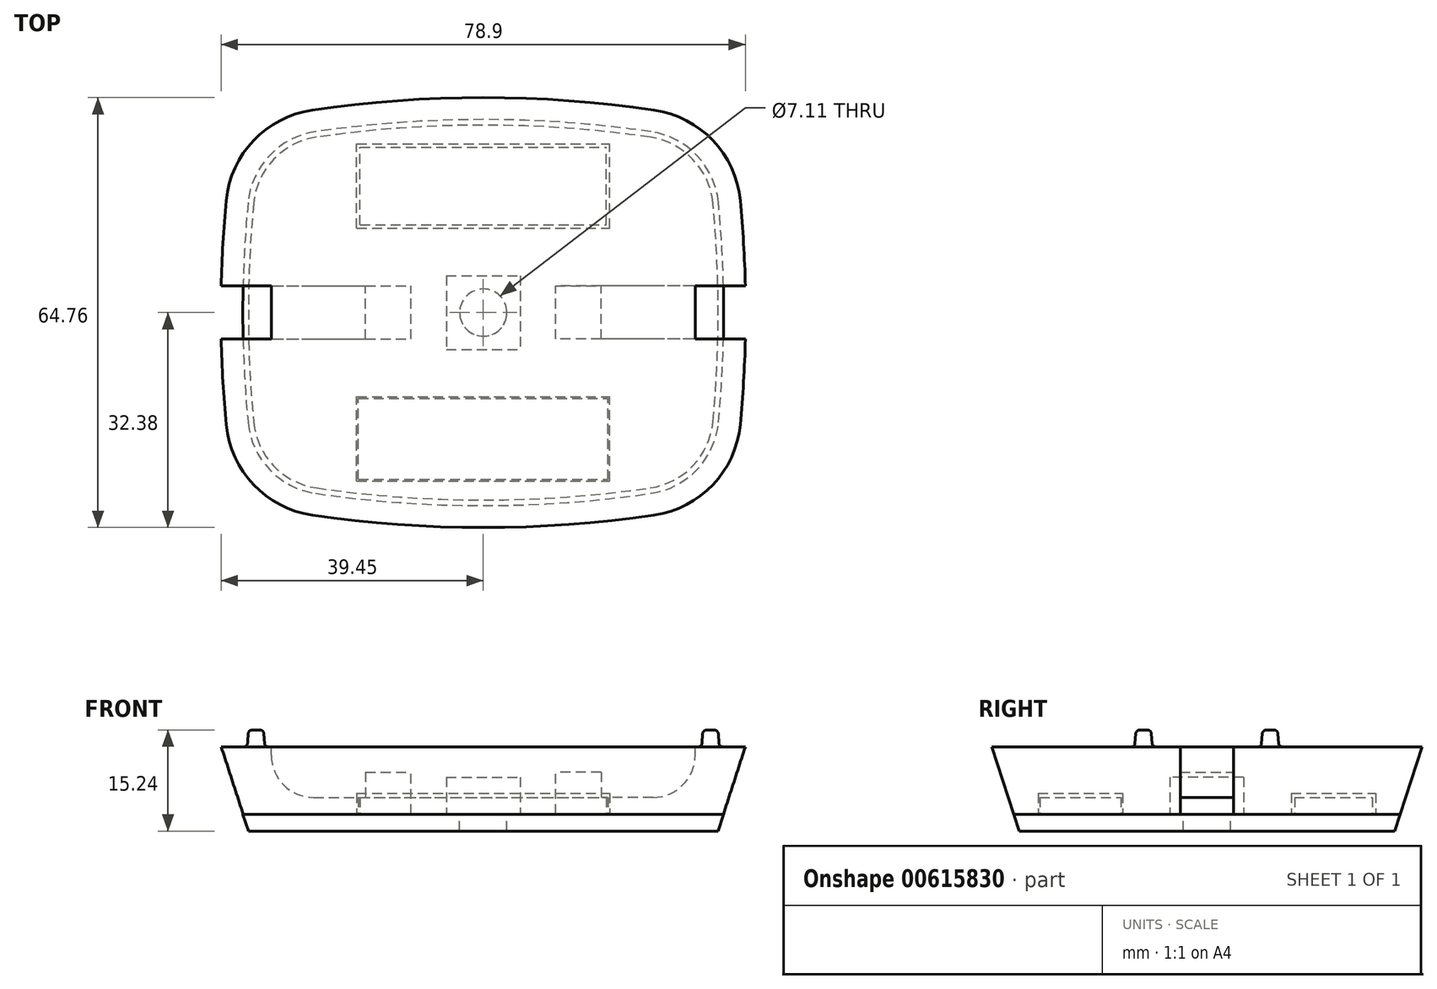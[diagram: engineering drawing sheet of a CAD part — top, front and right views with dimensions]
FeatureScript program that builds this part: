
annotation { "Feature Type Name" : "Feature", "Feature Type Description" : "" }
export const myFeature = defineFeature(function(context is Context, id is Id, definition is map)
    precondition{}
    {
        {
            var Q0;
            Q0=qCreatedBy(makeId("Top.planeOp"),FACE);
            var sketch = newSketch(context, id + "F0", { "sketchPlane" : qUnion([Q0])});
            skLineSegment(sketch, "E0.bottom", {"start": v(-39.5, -32.39) * mm, "end": v(39.5, -32.39) * mm, "construction": true});
            skLineSegment(sketch, "E0.top", {"start": v(-39.5, 32.39) * mm, "end": v(39.5, 32.39) * mm, "construction": true});
            skLineSegment(sketch, "E0.left", {"start": v(-39.5, -32.39) * mm, "end": v(-39.5, 32.39) * mm, "construction": true});
            skLineSegment(sketch, "E0.right", {"start": v(39.5, -32.39) * mm, "end": v(39.5, 32.39) * mm, "construction": true});
            skPoint(sketch, "E1", {"position": v(0, 32.39) * mm});
            skPoint(sketch, "E2", {"position": v(39.5, 0) * mm});
            skLineSegment(sketch, "E3.bottom", {"start": v(-39.45, -4) * mm, "end": v(-31.9, -4) * mm});
            skLineSegment(sketch, "E3.top", {"start": v(-39.45, 4) * mm, "end": v(-31.9, 4) * mm});
            skLineSegment(sketch, "E3.right", {"start": v(-31.9, -4) * mm, "end": v(-31.9, 4) * mm});
            skLineSegment(sketch, "E4.bottom", {"start": v(39.45, -4) * mm, "end": v(31.9, -4) * mm});
            skLineSegment(sketch, "E4.top", {"start": v(39.45, 4) * mm, "end": v(31.9, 4) * mm});
            skLineSegment(sketch, "E4.right", {"start": v(31.9, -4) * mm, "end": v(31.9, 4) * mm});
            skPoint(sketch, "E5", {"position": v(-31.9, 0) * mm});
            skPoint(sketch, "E6", {"position": v(31.9, 0) * mm});
            skPoint(sketch, "E7", {"position": v(0, 0) * mm});
            skArc(sketch, "E8", {"start": v(25.73, 30.51) * mm, "mid": v(0, 32.38) * mm, "end": v(-25.73, 30.51) * mm});
            skArc(sketch, "E9", {"start": v(-25.73, -30.51) * mm, "mid": v(0, -32.38) * mm, "end": v(25.73, -30.51) * mm});
            skPoint(sketch, "E10", {"position": v(0, -32.38) * mm});
            skArc(sketch, "E11", {"start": v(-38.7, 16.88) * mm, "mid": v(-39.19, 10.45) * mm, "end": v(-39.45, 4) * mm});
            skArc(sketch, "E12", {"start": v(38.7, -16.88) * mm, "mid": v(39.19, -10.45) * mm, "end": v(39.45, -4) * mm});
            skPoint(sketch, "E13", {"position": v(-39.5, 0) * mm});
            skArc(sketch, "E14.filletArc", {"start": v(-25.73, 30.51) * mm, "mid": v(-34.57, 25.94) * mm, "end": v(-38.7, 16.88) * mm});
            skArc(sketch, "E15.filletArc", {"start": v(38.7, 16.88) * mm, "mid": v(34.57, 25.94) * mm, "end": v(25.73, 30.51) * mm});
            skArc(sketch, "E16.filletArc", {"start": v(25.73, -30.51) * mm, "mid": v(34.57, -25.94) * mm, "end": v(38.7, -16.88) * mm});
            skArc(sketch, "E17.filletArc", {"start": v(-38.7, -16.88) * mm, "mid": v(-34.57, -25.94) * mm, "end": v(-25.73, -30.51) * mm});
            skArc(sketch, "E18.trimOffspring", {"start": v(39.45, 4) * mm, "mid": v(39.19, 10.45) * mm, "end": v(38.7, 16.88) * mm});
            skArc(sketch, "E19.trimOffspring", {"start": v(-39.45, -4) * mm, "mid": v(-39.19, -10.45) * mm, "end": v(-38.7, -16.88) * mm});
            skSolve(sketch);
        }
        {
            var Q0;
            Q0=qSketchRegion(id+"F0",true);
            extrude(context, id + "F1", {"entities" : qUnion([Q0]), "oppositeDirection" : true, "depth" : 7.62 * mm});
        }
        {
            var Q0;
            Q0=qCreatedBy(makeId("Top.planeOp"),FACE);
            var sketch = newSketch(context, id + "F2", { "sketchPlane" : qUnion([Q0])});
            skCircle(sketch, "E20", {"center": v(-34.2, 9.53) * mm, "radius": 1.4 * mm});
            skCircle(sketch, "E21", {"center": v(-34.2, -9.53) * mm, "radius": 1.4 * mm});
            skCircle(sketch, "E22", {"center": v(34.2, 9.53) * mm, "radius": 1.4 * mm});
            skCircle(sketch, "E23", {"center": v(34.2, -9.53) * mm, "radius": 1.4 * mm});
            skLineSegment(sketch, "E24", {"start": v(-34.2, 9.53) * mm, "end": v(34.2, 9.53) * mm, "construction": true});
            skPoint(sketch, "E25", {"position": v(0, 9.53) * mm});
            skLineSegment(sketch, "E26", {"start": v(-34.2, 9.53) * mm, "end": v(-34.2, -9.53) * mm, "construction": true});
            skPoint(sketch, "E27", {"position": v(-34.2, 0) * mm});
            skSolve(sketch);
        }
        {
            var Q0;
            Q0=qSketchRegion(id+"F2",true);
            extrude(context, id + "F3", {"entities" : qUnion([Q0]), "operationType" : NewBodyOperationType.ADD, "depth" : 2.54 * mm});
        }
        {
            var Q0;
            Q0=makeQuery(id+"F3.opExtrude","CAP_EDGE",EDGE,{"disambiguationData":[OSD([sQuery(id+"F2.wireOp",EDGE,"E20")])],"isStart":false});
            var Q1;
            Q1=makeQuery(id+"F3.opExtrude","CAP_EDGE",EDGE,{"disambiguationData":[OSD([sQuery(id+"F2.wireOp",EDGE,"E21")])],"isStart":false});
            var Q2;
            Q2=makeQuery(id+"F3.opExtrude","CAP_EDGE",EDGE,{"disambiguationData":[OSD([sQuery(id+"F2.wireOp",EDGE,"E22")])],"isStart":false});
            var Q3;
            Q3=makeQuery(id+"F3.opExtrude","CAP_EDGE",EDGE,{"disambiguationData":[OSD([sQuery(id+"F2.wireOp",EDGE,"E23")])],"isStart":false});
            chamfer(context, id + "F4", {"entities" : qUnion([Q0, Q1, Q2, Q3]), "chamferType" : ChamferType.TWO_OFFSETS, "width1" : 0.25 * mm, "oppositeDirection" : false, "width2" : 3.56 * mm, "tangentPropagation" : true});
        }
        {
            var Q0;
            {var subQ0=sQuery(id+"F2.wireOp",EDGE,"E20");Q0=makeQuery(id+"F4.opChamfer","BLEND_EDGE",EDGE,{"blendedFrom":[makeQuery(id+"F3.opExtrude","CAP_EDGE",EDGE,{"disambiguationData":[OSD([subQ0])],"isStart":false}),makeQuery(id+"F3.opExtrude","CAP_FACE",FACE,{"disambiguationData":[OSD([subQ0])],"isStart":false})],"blendedInto":[makeQuery(id+"F3.opExtrude","CAP_FACE",FACE,{"disambiguationData":[OSD([subQ0])],"isStart":false})]});}
            var Q1;
            {var subQ0=sQuery(id+"F2.wireOp",EDGE,"E21");Q1=makeQuery(id+"F4.opChamfer","BLEND_EDGE",EDGE,{"blendedFrom":[makeQuery(id+"F3.opExtrude","CAP_EDGE",EDGE,{"disambiguationData":[OSD([subQ0])],"isStart":false}),makeQuery(id+"F3.opExtrude","CAP_FACE",FACE,{"disambiguationData":[OSD([subQ0])],"isStart":false})],"blendedInto":[makeQuery(id+"F3.opExtrude","CAP_FACE",FACE,{"disambiguationData":[OSD([subQ0])],"isStart":false})]});}
            var Q2;
            {var subQ0=sQuery(id+"F2.wireOp",EDGE,"E22");Q2=makeQuery(id+"F4.opChamfer","BLEND_EDGE",EDGE,{"blendedFrom":[makeQuery(id+"F3.opExtrude","CAP_EDGE",EDGE,{"disambiguationData":[OSD([subQ0])],"isStart":false}),makeQuery(id+"F3.opExtrude","CAP_FACE",FACE,{"disambiguationData":[OSD([subQ0])],"isStart":false})],"blendedInto":[makeQuery(id+"F3.opExtrude","CAP_FACE",FACE,{"disambiguationData":[OSD([subQ0])],"isStart":false})]});}
            var Q3;
            {var subQ0=sQuery(id+"F2.wireOp",EDGE,"E23");Q3=makeQuery(id+"F4.opChamfer","BLEND_EDGE",EDGE,{"blendedFrom":[makeQuery(id+"F3.opExtrude","CAP_EDGE",EDGE,{"disambiguationData":[OSD([subQ0])],"isStart":false}),makeQuery(id+"F3.opExtrude","CAP_FACE",FACE,{"disambiguationData":[OSD([subQ0])],"isStart":false})],"blendedInto":[makeQuery(id+"F3.opExtrude","CAP_FACE",FACE,{"disambiguationData":[OSD([subQ0])],"isStart":false})]});}
            fillet(context, id + "F5", {"entities" : qUnion([Q0, Q1, Q2, Q3]), "radius" : 0.64 * mm, "tangentPropagation" : true, "allowEdgeOverflow" : false});
        }
        {
            var Q0;
            Q0=makeQuery(id+"F4.opChamfer","BLEND_EDGE",EDGE,{"blendedFrom":[makeQuery(id+"F3.opExtrude","CAP_EDGE",EDGE,{"disambiguationData":[OSD([sQuery(id+"F2.wireOp",EDGE,"E20")])],"isStart":false}),makeQuery(id+"F1.opExtrude","CAP_FACE",FACE,{"disambiguationData":[OSD([sQuery(id+"F0.wireOp",EDGE,"E3.bottom"),sQuery(id+"F0.wireOp",EDGE,"E3.top"),sQuery(id+"F0.wireOp",EDGE,"E3.left"),sQuery(id+"F0.wireOp",EDGE,"E3.right"),sQuery(id+"F0.wireOp",EDGE,"E4.bottom"),sQuery(id+"F0.wireOp",EDGE,"E4.top"),sQuery(id+"F0.wireOp",EDGE,"E4.left"),sQuery(id+"F0.wireOp",EDGE,"E4.right"),sQuery(id+"F0.wireOp",EDGE,"E8"),sQuery(id+"F0.wireOp",EDGE,"E9"),sQuery(id+"F0.wireOp",EDGE,"E11"),sQuery(id+"F0.wireOp",EDGE,"E12"),sQuery(id+"F0.wireOp",EDGE,"E14.filletArc"),sQuery(id+"F0.wireOp",EDGE,"E15.filletArc"),sQuery(id+"F0.wireOp",EDGE,"E16.filletArc"),sQuery(id+"F0.wireOp",EDGE,"E17.filletArc")])],"isStart":true})],"blendedInto":[makeQuery(id+"F1.opExtrude","CAP_FACE",FACE,{"disambiguationData":[OSD([sQuery(id+"F0.wireOp",EDGE,"E3.bottom"),sQuery(id+"F0.wireOp",EDGE,"E3.top"),sQuery(id+"F0.wireOp",EDGE,"E3.left"),sQuery(id+"F0.wireOp",EDGE,"E3.right"),sQuery(id+"F0.wireOp",EDGE,"E4.bottom"),sQuery(id+"F0.wireOp",EDGE,"E4.top"),sQuery(id+"F0.wireOp",EDGE,"E4.left"),sQuery(id+"F0.wireOp",EDGE,"E4.right"),sQuery(id+"F0.wireOp",EDGE,"E8"),sQuery(id+"F0.wireOp",EDGE,"E9"),sQuery(id+"F0.wireOp",EDGE,"E11"),sQuery(id+"F0.wireOp",EDGE,"E12"),sQuery(id+"F0.wireOp",EDGE,"E14.filletArc"),sQuery(id+"F0.wireOp",EDGE,"E15.filletArc"),sQuery(id+"F0.wireOp",EDGE,"E16.filletArc"),sQuery(id+"F0.wireOp",EDGE,"E17.filletArc")])],"isStart":true})]});
            var Q1;
            Q1=makeQuery(id+"F4.opChamfer","BLEND_EDGE",EDGE,{"blendedFrom":[makeQuery(id+"F3.opExtrude","CAP_EDGE",EDGE,{"disambiguationData":[OSD([sQuery(id+"F2.wireOp",EDGE,"E21")])],"isStart":false}),makeQuery(id+"F1.opExtrude","CAP_FACE",FACE,{"disambiguationData":[OSD([sQuery(id+"F0.wireOp",EDGE,"E3.bottom"),sQuery(id+"F0.wireOp",EDGE,"E3.top"),sQuery(id+"F0.wireOp",EDGE,"E3.left"),sQuery(id+"F0.wireOp",EDGE,"E3.right"),sQuery(id+"F0.wireOp",EDGE,"E4.bottom"),sQuery(id+"F0.wireOp",EDGE,"E4.top"),sQuery(id+"F0.wireOp",EDGE,"E4.left"),sQuery(id+"F0.wireOp",EDGE,"E4.right"),sQuery(id+"F0.wireOp",EDGE,"E8"),sQuery(id+"F0.wireOp",EDGE,"E9"),sQuery(id+"F0.wireOp",EDGE,"E11"),sQuery(id+"F0.wireOp",EDGE,"E12"),sQuery(id+"F0.wireOp",EDGE,"E14.filletArc"),sQuery(id+"F0.wireOp",EDGE,"E15.filletArc"),sQuery(id+"F0.wireOp",EDGE,"E16.filletArc"),sQuery(id+"F0.wireOp",EDGE,"E17.filletArc")])],"isStart":true})],"blendedInto":[makeQuery(id+"F1.opExtrude","CAP_FACE",FACE,{"disambiguationData":[OSD([sQuery(id+"F0.wireOp",EDGE,"E3.bottom"),sQuery(id+"F0.wireOp",EDGE,"E3.top"),sQuery(id+"F0.wireOp",EDGE,"E3.left"),sQuery(id+"F0.wireOp",EDGE,"E3.right"),sQuery(id+"F0.wireOp",EDGE,"E4.bottom"),sQuery(id+"F0.wireOp",EDGE,"E4.top"),sQuery(id+"F0.wireOp",EDGE,"E4.left"),sQuery(id+"F0.wireOp",EDGE,"E4.right"),sQuery(id+"F0.wireOp",EDGE,"E8"),sQuery(id+"F0.wireOp",EDGE,"E9"),sQuery(id+"F0.wireOp",EDGE,"E11"),sQuery(id+"F0.wireOp",EDGE,"E12"),sQuery(id+"F0.wireOp",EDGE,"E14.filletArc"),sQuery(id+"F0.wireOp",EDGE,"E15.filletArc"),sQuery(id+"F0.wireOp",EDGE,"E16.filletArc"),sQuery(id+"F0.wireOp",EDGE,"E17.filletArc")])],"isStart":true})]});
            var Q2;
            Q2=makeQuery(id+"F4.opChamfer","BLEND_EDGE",EDGE,{"blendedFrom":[makeQuery(id+"F3.opExtrude","CAP_EDGE",EDGE,{"disambiguationData":[OSD([sQuery(id+"F2.wireOp",EDGE,"E22")])],"isStart":false}),makeQuery(id+"F1.opExtrude","CAP_FACE",FACE,{"disambiguationData":[OSD([sQuery(id+"F0.wireOp",EDGE,"E3.bottom"),sQuery(id+"F0.wireOp",EDGE,"E3.top"),sQuery(id+"F0.wireOp",EDGE,"E3.left"),sQuery(id+"F0.wireOp",EDGE,"E3.right"),sQuery(id+"F0.wireOp",EDGE,"E4.bottom"),sQuery(id+"F0.wireOp",EDGE,"E4.top"),sQuery(id+"F0.wireOp",EDGE,"E4.left"),sQuery(id+"F0.wireOp",EDGE,"E4.right"),sQuery(id+"F0.wireOp",EDGE,"E8"),sQuery(id+"F0.wireOp",EDGE,"E9"),sQuery(id+"F0.wireOp",EDGE,"E11"),sQuery(id+"F0.wireOp",EDGE,"E12"),sQuery(id+"F0.wireOp",EDGE,"E14.filletArc"),sQuery(id+"F0.wireOp",EDGE,"E15.filletArc"),sQuery(id+"F0.wireOp",EDGE,"E16.filletArc"),sQuery(id+"F0.wireOp",EDGE,"E17.filletArc")])],"isStart":true})],"blendedInto":[makeQuery(id+"F1.opExtrude","CAP_FACE",FACE,{"disambiguationData":[OSD([sQuery(id+"F0.wireOp",EDGE,"E3.bottom"),sQuery(id+"F0.wireOp",EDGE,"E3.top"),sQuery(id+"F0.wireOp",EDGE,"E3.left"),sQuery(id+"F0.wireOp",EDGE,"E3.right"),sQuery(id+"F0.wireOp",EDGE,"E4.bottom"),sQuery(id+"F0.wireOp",EDGE,"E4.top"),sQuery(id+"F0.wireOp",EDGE,"E4.left"),sQuery(id+"F0.wireOp",EDGE,"E4.right"),sQuery(id+"F0.wireOp",EDGE,"E8"),sQuery(id+"F0.wireOp",EDGE,"E9"),sQuery(id+"F0.wireOp",EDGE,"E11"),sQuery(id+"F0.wireOp",EDGE,"E12"),sQuery(id+"F0.wireOp",EDGE,"E14.filletArc"),sQuery(id+"F0.wireOp",EDGE,"E15.filletArc"),sQuery(id+"F0.wireOp",EDGE,"E16.filletArc"),sQuery(id+"F0.wireOp",EDGE,"E17.filletArc")])],"isStart":true})]});
            var Q3;
            Q3=makeQuery(id+"F4.opChamfer","BLEND_EDGE",EDGE,{"blendedFrom":[makeQuery(id+"F3.opExtrude","CAP_EDGE",EDGE,{"disambiguationData":[OSD([sQuery(id+"F2.wireOp",EDGE,"E23")])],"isStart":false}),makeQuery(id+"F1.opExtrude","CAP_FACE",FACE,{"disambiguationData":[OSD([sQuery(id+"F0.wireOp",EDGE,"E3.bottom"),sQuery(id+"F0.wireOp",EDGE,"E3.top"),sQuery(id+"F0.wireOp",EDGE,"E3.left"),sQuery(id+"F0.wireOp",EDGE,"E3.right"),sQuery(id+"F0.wireOp",EDGE,"E4.bottom"),sQuery(id+"F0.wireOp",EDGE,"E4.top"),sQuery(id+"F0.wireOp",EDGE,"E4.left"),sQuery(id+"F0.wireOp",EDGE,"E4.right"),sQuery(id+"F0.wireOp",EDGE,"E8"),sQuery(id+"F0.wireOp",EDGE,"E9"),sQuery(id+"F0.wireOp",EDGE,"E11"),sQuery(id+"F0.wireOp",EDGE,"E12"),sQuery(id+"F0.wireOp",EDGE,"E14.filletArc"),sQuery(id+"F0.wireOp",EDGE,"E15.filletArc"),sQuery(id+"F0.wireOp",EDGE,"E16.filletArc"),sQuery(id+"F0.wireOp",EDGE,"E17.filletArc")])],"isStart":true})],"blendedInto":[makeQuery(id+"F1.opExtrude","CAP_FACE",FACE,{"disambiguationData":[OSD([sQuery(id+"F0.wireOp",EDGE,"E3.bottom"),sQuery(id+"F0.wireOp",EDGE,"E3.top"),sQuery(id+"F0.wireOp",EDGE,"E3.left"),sQuery(id+"F0.wireOp",EDGE,"E3.right"),sQuery(id+"F0.wireOp",EDGE,"E4.bottom"),sQuery(id+"F0.wireOp",EDGE,"E4.top"),sQuery(id+"F0.wireOp",EDGE,"E4.left"),sQuery(id+"F0.wireOp",EDGE,"E4.right"),sQuery(id+"F0.wireOp",EDGE,"E8"),sQuery(id+"F0.wireOp",EDGE,"E9"),sQuery(id+"F0.wireOp",EDGE,"E11"),sQuery(id+"F0.wireOp",EDGE,"E12"),sQuery(id+"F0.wireOp",EDGE,"E14.filletArc"),sQuery(id+"F0.wireOp",EDGE,"E15.filletArc"),sQuery(id+"F0.wireOp",EDGE,"E16.filletArc"),sQuery(id+"F0.wireOp",EDGE,"E17.filletArc")])],"isStart":true})]});
            fillet(context, id + "F6", {"entities" : qUnion([Q0, Q1, Q2, Q3]), "radius" : 0.5 * mm, "tangentPropagation" : true, "allowEdgeOverflow" : false});
        }
        {
            var Q0;
            Q0=makeQuery(id+"F1.opExtrude","CAP_FACE",FACE,{"disambiguationData":[OSD([sQuery(id+"F0.wireOp",EDGE,"E3.bottom"),sQuery(id+"F0.wireOp",EDGE,"E3.top"),sQuery(id+"F0.wireOp",EDGE,"E3.left"),sQuery(id+"F0.wireOp",EDGE,"E3.right"),sQuery(id+"F0.wireOp",EDGE,"E4.bottom"),sQuery(id+"F0.wireOp",EDGE,"E4.top"),sQuery(id+"F0.wireOp",EDGE,"E4.left"),sQuery(id+"F0.wireOp",EDGE,"E4.right"),sQuery(id+"F0.wireOp",EDGE,"E8"),sQuery(id+"F0.wireOp",EDGE,"E9"),sQuery(id+"F0.wireOp",EDGE,"E11"),sQuery(id+"F0.wireOp",EDGE,"E12"),sQuery(id+"F0.wireOp",EDGE,"E14.filletArc"),sQuery(id+"F0.wireOp",EDGE,"E15.filletArc"),sQuery(id+"F0.wireOp",EDGE,"E16.filletArc"),sQuery(id+"F0.wireOp",EDGE,"E17.filletArc")])],"isStart":false});
            var sketch = newSketch(context, id + "F7", { "sketchPlane" : qUnion([Q0])});
            skArc(sketch, "E28.0", {"start": v(-38.7, 16.88) * mm, "mid": v(-34.57, 25.94) * mm, "end": v(-25.73, 30.51) * mm});
            skArc(sketch, "E28.1", {"start": v(-25.73, 30.51) * mm, "mid": v(0, 32.38) * mm, "end": v(25.73, 30.51) * mm});
            skArc(sketch, "E28.2", {"start": v(25.73, 30.51) * mm, "mid": v(34.57, 25.94) * mm, "end": v(38.7, 16.88) * mm});
            skArc(sketch, "E28.8", {"start": v(25.73, -30.51) * mm, "mid": v(0, -32.38) * mm, "end": v(-25.73, -30.51) * mm});
            skArc(sketch, "E28.9", {"start": v(-25.73, -30.51) * mm, "mid": v(-34.57, -25.94) * mm, "end": v(-38.7, -16.88) * mm});
            skLineSegment(sketch, "E29", {"start": v(-10.87, 4) * mm, "end": v(-10.87, -4) * mm});
            skLineSegment(sketch, "E30", {"start": v(10.87, 4) * mm, "end": v(10.87, -4) * mm});
            skArc(sketch, "E31.0", {"start": v(38.7, -16.88) * mm, "mid": v(34.57, -25.94) * mm, "end": v(25.73, -30.51) * mm});
            skArc(sketch, "E32.0", {"start": v(-38.7, -16.88) * mm, "mid": v(-39.19, -10.45) * mm, "end": v(-39.45, -4) * mm});
            skLineSegment(sketch, "E33.0", {"start": v(-39.45, -4) * mm, "end": v(-10.87, -4) * mm});
            skArc(sketch, "E34.0", {"start": v(39.45, -4) * mm, "mid": v(39.19, -10.45) * mm, "end": v(38.7, -16.88) * mm});
            skLineSegment(sketch, "E35.0", {"start": v(39.45, -4) * mm, "end": v(10.87, -4) * mm});
            skArc(sketch, "E36.0", {"start": v(38.7, 16.88) * mm, "mid": v(39.19, 10.45) * mm, "end": v(39.45, 4) * mm});
            skLineSegment(sketch, "E37.0", {"start": v(39.45, 4) * mm, "end": v(10.87, 4) * mm});
            skArc(sketch, "E38.0", {"start": v(-39.45, 4) * mm, "mid": v(-39.19, 10.45) * mm, "end": v(-38.7, 16.88) * mm});
            skLineSegment(sketch, "E39.0", {"start": v(-39.45, 4) * mm, "end": v(-10.87, 4) * mm});
            skSolve(sketch);
        }
        {
            var Q0;
            Q0=qSketchRegion(id+"F7",true);
            extrude(context, id + "F8", {"entities" : qUnion([Q0]), "operationType" : NewBodyOperationType.ADD, "depth" : 2.54 * mm});
        }
        {
            var Q0;
            {var subQ0=sQuery(id+"F0.wireOp",EDGE,"E3.bottom");var subQ1=sQuery(id+"F0.wireOp",EDGE,"E3.top");var subQ2=sQuery(id+"F0.wireOp",EDGE,"E3.right");Q0=makeQuery(id+"F8.boolean.opBoolean","SPLIT",FACE,{"disambiguationData":[TD([makeQuery(id+"F1.opExtrude","SWEPT_FACE",FACE,{"disambiguationData":[OSD([subQ0])]})])],"derivedFrom":makeQuery(id+"F1.opExtrude","CAP_FACE",FACE,{"disambiguationData":[OSD([subQ0,subQ1,subQ2,sQuery(id+"F0.wireOp",EDGE,"E4.bottom"),sQuery(id+"F0.wireOp",EDGE,"E4.top"),sQuery(id+"F0.wireOp",EDGE,"E4.right"),sQuery(id+"F0.wireOp",EDGE,"E8"),sQuery(id+"F0.wireOp",EDGE,"E9"),sQuery(id+"F0.wireOp",EDGE,"E11"),sQuery(id+"F0.wireOp",EDGE,"E12"),sQuery(id+"F0.wireOp",EDGE,"E14.filletArc"),sQuery(id+"F0.wireOp",EDGE,"E15.filletArc"),sQuery(id+"F0.wireOp",EDGE,"E16.filletArc"),sQuery(id+"F0.wireOp",EDGE,"E17.filletArc"),sQuery(id+"F0.wireOp",EDGE,"E18.trimOffspring"),sQuery(id+"F0.wireOp",EDGE,"E19.trimOffspring")])],"isStart":false})});}
            var sketch = newSketch(context, id + "F9", { "sketchPlane" : qUnion([Q0])});
            skLineSegment(sketch, "E40.0.0", {"start": v(-10.87, 4) * mm, "end": v(-17.73, 4) * mm});
            skLineSegment(sketch, "E40.0.2", {"start": v(-17.73, -4) * mm, "end": v(-10.87, -4) * mm});
            skLineSegment(sketch, "E40.0.3", {"start": v(-10.87, -4) * mm, "end": v(-10.87, 4) * mm});
            skLineSegment(sketch, "E41.0.0", {"start": v(10.87, -4) * mm, "end": v(17.73, -4) * mm});
            skLineSegment(sketch, "E41.0.2", {"start": v(17.73, 4) * mm, "end": v(10.87, 4) * mm});
            skLineSegment(sketch, "E41.0.3", {"start": v(10.87, 4) * mm, "end": v(10.87, -4) * mm});
            skLineSegment(sketch, "E42", {"start": v(-17.73, 4) * mm, "end": v(-17.73, -4) * mm});
            skLineSegment(sketch, "E43", {"start": v(17.73, 4) * mm, "end": v(17.73, -4) * mm});
            skSolve(sketch);
        }
        {
            var Q0;
            Q0=qSketchRegion(id+"F9",true);
            extrude(context, id + "F10", {"entities" : qUnion([Q0]), "operationType" : NewBodyOperationType.REMOVE, "oppositeDirection" : true, "depth" : 3.8 * mm});
        }
        {
            var Q0;
            Q0=makeQuery(id+"F1.opExtrude","CAP_EDGE",EDGE,{"disambiguationData":[OSD([sQuery(id+"F0.wireOp",EDGE,"E3.right")])],"isStart":false});
            var Q1;
            Q1=makeQuery(id+"F1.opExtrude","CAP_EDGE",EDGE,{"disambiguationData":[OSD([sQuery(id+"F0.wireOp",EDGE,"E4.right")])],"isStart":false});
            fillet(context, id + "F11", {"entities" : qUnion([Q0, Q1]), "radius" : 6.35 * mm, "tangentPropagation" : true, "allowEdgeOverflow" : false});
        }
        {
            var Q0;
            Q0=makeQuery(id+"F8.opExtrude","CAP_EDGE",EDGE,{"disambiguationData":[OSD([sQuery(id+"F7.wireOp",EDGE,"E28.9")])],"isStart":false});
            var Q1;
            Q1=makeQuery(id+"F8.opExtrude","CAP_EDGE",EDGE,{"disambiguationData":[OSD([sQuery(id+"F7.wireOp",EDGE,"E28.0")])],"isStart":false});
            chamfer(context, id + "F12", {"entities" : qUnion([Q0, Q1]), "chamferType" : ChamferType.TWO_OFFSETS, "width1" : 10.16 * mm, "oppositeDirection" : false, "width2" : 3.3 * mm, "tangentPropagation" : true});
        }
        {
            var Q0;
            Q0=makeQuery(id+"F8.opExtrude","CAP_FACE",FACE,{"disambiguationData":[OSD([sQuery(id+"F7.wireOp",EDGE,"E28.0"),sQuery(id+"F7.wireOp",EDGE,"E28.1"),sQuery(id+"F7.wireOp",EDGE,"E28.2"),sQuery(id+"F7.wireOp",EDGE,"E28.3"),sQuery(id+"F7.wireOp",EDGE,"E28.4"),sQuery(id+"F7.wireOp",EDGE,"E28.11")])],"isStart":false});
            var sketch = newSketch(context, id + "F13", { "sketchPlane" : qUnion([Q0])});
            skArc(sketch, "E44.0.2", {"start": v(35.4, 16.57) * mm, "mid": v(32.17, 23.66) * mm, "end": v(25.25, 27.25) * mm});
            skArc(sketch, "E44.0.3", {"start": v(25.25, 27.25) * mm, "mid": v(0, 29.08) * mm, "end": v(-25.25, 27.25) * mm});
            skArc(sketch, "E44.0.4", {"start": v(-25.25, 27.25) * mm, "mid": v(-32.17, 23.66) * mm, "end": v(-35.4, 16.57) * mm});
            skArc(sketch, "E44.0.9", {"start": v(-35.4, 16.57) * mm, "mid": v(-36.2, 0) * mm, "end": v(-35.4, -16.57) * mm});
            skArc(sketch, "E44.0.10", {"start": v(-35.4, -16.57) * mm, "mid": v(-32.17, -23.66) * mm, "end": v(-25.25, -27.25) * mm});
            skArc(sketch, "E44.0.11", {"start": v(-25.25, -27.25) * mm, "mid": v(0, -29.08) * mm, "end": v(25.25, -27.25) * mm});
            skArc(sketch, "E44.0.12", {"start": v(25.25, -27.25) * mm, "mid": v(32.17, -23.66) * mm, "end": v(35.4, -16.57) * mm});
            skArc(sketch, "E44.0.13", {"start": v(35.4, -16.57) * mm, "mid": v(36.2, 0) * mm, "end": v(35.4, 16.57) * mm});
            skSolve(sketch);
        }
        {
            var Q0;
            Q0=qSketchRegion(id+"F13",true);
            extrude(context, id + "F14", {"entities" : qUnion([Q0]), "depth" : 2.54 * mm});
        }
        {
            var Q0;
            Q0=makeQuery(id+"F14.opExtrude","CAP_EDGE",EDGE,{"disambiguationData":[OSD([sQuery(id+"F13.wireOp",EDGE,"E44.0.3")])],"isStart":false});
            chamfer(context, id + "F15", {"entities" : qUnion([Q0]), "chamferType" : ChamferType.TWO_OFFSETS, "width1" : 0.84 * mm, "oppositeDirection" : false, "width2" : 2.54 * mm, "tangentPropagation" : true});
        }
        {
            var Q0;
            Q0=makeQuery(id+"F8.opExtrude","CAP_FACE",FACE,{"disambiguationData":[OSD([sQuery(id+"F7.wireOp",EDGE,"E28.0"),sQuery(id+"F7.wireOp",EDGE,"E28.1"),sQuery(id+"F7.wireOp",EDGE,"E28.2"),sQuery(id+"F7.wireOp",EDGE,"E28.3"),sQuery(id+"F7.wireOp",EDGE,"E28.4"),sQuery(id+"F7.wireOp",EDGE,"E28.11")])],"isStart":false});
            var sketch = newSketch(context, id + "F16", { "sketchPlane" : qUnion([Q0])});
            skLineSegment(sketch, "E45.bottom", {"start": v(-19.05, 25.4) * mm, "end": v(19.05, 25.4) * mm});
            skLineSegment(sketch, "E45.top", {"start": v(-19.05, 12.7) * mm, "end": v(19.05, 12.7) * mm});
            skLineSegment(sketch, "E45.left", {"start": v(-19.05, 25.4) * mm, "end": v(-19.05, 12.7) * mm});
            skLineSegment(sketch, "E45.right", {"start": v(19.05, 25.4) * mm, "end": v(19.05, 12.7) * mm});
            skLineSegment(sketch, "E46.bottom", {"start": v(-19.05, -12.7) * mm, "end": v(19.05, -12.7) * mm});
            skLineSegment(sketch, "E46.top", {"start": v(-19.05, -25.4) * mm, "end": v(19.05, -25.4) * mm});
            skLineSegment(sketch, "E46.left", {"start": v(-19.05, -12.7) * mm, "end": v(-19.05, -25.4) * mm});
            skLineSegment(sketch, "E46.right", {"start": v(19.05, -12.7) * mm, "end": v(19.05, -25.4) * mm});
            skPoint(sketch, "E47", {"position": v(0, -12.7) * mm});
            skPoint(sketch, "E48", {"position": v(0, 12.7) * mm});
            skLineSegment(sketch, "E49", {"start": v(0, 12.7) * mm, "end": v(0, -12.7) * mm, "construction": true});
            skPoint(sketch, "E50", {"position": v(0, 0) * mm});
            skSolve(sketch);
        }
        {
            var Q0;
            Q0=qSketchRegion(id+"F16",true);
            extrude(context, id + "F17", {"entities" : qUnion([Q0]), "operationType" : NewBodyOperationType.REMOVE, "oppositeDirection" : true, "depth" : 3.17 * mm});
        }
        {
            var Q0;
            Q0=makeQuery(id+"F14.opExtrude","CAP_FACE",FACE,{"disambiguationData":[OSD([sQuery(id+"F13.wireOp",EDGE,"E44.0.2"),sQuery(id+"F13.wireOp",EDGE,"E44.0.3"),sQuery(id+"F13.wireOp",EDGE,"E44.0.4"),sQuery(id+"F13.wireOp",EDGE,"E44.0.9"),sQuery(id+"F13.wireOp",EDGE,"E44.0.10"),sQuery(id+"F13.wireOp",EDGE,"E44.0.11"),sQuery(id+"F13.wireOp",EDGE,"E44.0.12"),sQuery(id+"F13.wireOp",EDGE,"E44.0.13")])],"isStart":true});
            var sketch = newSketch(context, id + "F18", { "sketchPlane" : qUnion([Q0])});
            skLineSegment(sketch, "E51.0", {"start": v(-19.05, 12.7) * mm, "end": v(-19.05, 25.4) * mm, "construction": true});
            skLineSegment(sketch, "E51.1", {"start": v(-19.05, 25.4) * mm, "end": v(19.05, 25.4) * mm, "construction": true});
            skLineSegment(sketch, "E51.2", {"start": v(19.05, 12.7) * mm, "end": v(19.05, 25.4) * mm, "construction": true});
            skLineSegment(sketch, "E51.3", {"start": v(-19.05, 12.7) * mm, "end": v(19.05, 12.7) * mm, "construction": true});
            skLineSegment(sketch, "E51.4", {"start": v(-19.05, -12.7) * mm, "end": v(19.05, -12.7) * mm, "construction": true});
            skLineSegment(sketch, "E51.5", {"start": v(19.05, -25.4) * mm, "end": v(19.05, -12.7) * mm, "construction": true});
            skLineSegment(sketch, "E51.6", {"start": v(-19.05, -25.4) * mm, "end": v(19.05, -25.4) * mm, "construction": true});
            skLineSegment(sketch, "E51.7", {"start": v(-19.05, -25.4) * mm, "end": v(-19.05, -12.7) * mm, "construction": true});
            skLineSegment(sketch, "E52.0", {"start": v(-18.54, 24.9) * mm, "end": v(18.54, 24.9) * mm});
            skLineSegment(sketch, "E52.1", {"start": v(-18.54, 13.2) * mm, "end": v(-18.54, 24.9) * mm});
            skLineSegment(sketch, "E52.2", {"start": v(-18.54, 13.2) * mm, "end": v(18.54, 13.2) * mm});
            skLineSegment(sketch, "E52.3", {"start": v(18.54, 13.2) * mm, "end": v(18.54, 24.9) * mm});
            skLineSegment(sketch, "E53.0", {"start": v(-18.8, -12.95) * mm, "end": v(18.8, -12.95) * mm});
            skLineSegment(sketch, "E53.1", {"start": v(-18.8, -25.15) * mm, "end": v(-18.8, -12.95) * mm});
            skLineSegment(sketch, "E53.2", {"start": v(-18.8, -25.15) * mm, "end": v(18.8, -25.15) * mm});
            skLineSegment(sketch, "E53.3", {"start": v(18.8, -25.15) * mm, "end": v(18.8, -12.95) * mm});
            skSolve(sketch);
        }
        {
            var Q0;
            Q0=qSketchRegion(id+"F18",true);
            extrude(context, id + "F19", {"entities" : qUnion([Q0]), "operationType" : NewBodyOperationType.ADD, "depth" : 2.54 * mm});
        }
        {
            var Q0;
            Q0=makeQuery(id+"F8.opExtrude","CAP_FACE",FACE,{"disambiguationData":[OSD([sQuery(id+"F7.wireOp",EDGE,"E28.0"),sQuery(id+"F7.wireOp",EDGE,"E28.1"),sQuery(id+"F7.wireOp",EDGE,"E28.2"),sQuery(id+"F7.wireOp",EDGE,"E28.3"),sQuery(id+"F7.wireOp",EDGE,"E28.4"),sQuery(id+"F7.wireOp",EDGE,"E28.11")])],"isStart":false});
            var sketch = newSketch(context, id + "F20", { "sketchPlane" : qUnion([Q0])});
            skLineSegment(sketch, "E54.bottom", {"start": v(-5.56, -5.56) * mm, "end": v(5.56, -5.56) * mm});
            skLineSegment(sketch, "E54.top", {"start": v(-5.56, 5.56) * mm, "end": v(5.56, 5.56) * mm});
            skLineSegment(sketch, "E54.left", {"start": v(-5.56, -5.56) * mm, "end": v(-5.56, 5.56) * mm});
            skLineSegment(sketch, "E54.right", {"start": v(5.56, -5.56) * mm, "end": v(5.56, 5.56) * mm});
            skPoint(sketch, "E55", {"position": v(0, 5.56) * mm});
            skPoint(sketch, "E56", {"position": v(5.56, 0) * mm});
            skSolve(sketch);
        }
        {
            var Q0;
            Q0=qSketchRegion(id+"F20",true);
            extrude(context, id + "F21", {"entities" : qUnion([Q0]), "operationType" : NewBodyOperationType.REMOVE, "oppositeDirection" : true, "depth" : 5.6 * mm});
        }
        {
            var Q0;
            Q0=makeQuery(id+"F14.opExtrude","CAP_FACE",FACE,{"disambiguationData":[OSD([sQuery(id+"F13.wireOp",EDGE,"E44.0.2"),sQuery(id+"F13.wireOp",EDGE,"E44.0.3"),sQuery(id+"F13.wireOp",EDGE,"E44.0.4"),sQuery(id+"F13.wireOp",EDGE,"E44.0.9"),sQuery(id+"F13.wireOp",EDGE,"E44.0.10"),sQuery(id+"F13.wireOp",EDGE,"E44.0.11"),sQuery(id+"F13.wireOp",EDGE,"E44.0.12"),sQuery(id+"F13.wireOp",EDGE,"E44.0.13")])],"isStart":true});
            var sketch = newSketch(context, id + "F22", { "sketchPlane" : qUnion([Q0])});
            skCircle(sketch, "E57", {"center": v(0, 0) * mm, "radius": 3.56 * mm});
            skSolve(sketch);
        }
        {
            var Q0;
            Q0=qSketchRegion(id+"F22",true);
            extrude(context, id + "F23", {"entities" : qUnion([Q0]), "operationType" : NewBodyOperationType.REMOVE, "endBound" : BoundingType.THROUGH_ALL, "oppositeDirection" : true, "depth" : 25.4 * mm});
        }
    });
